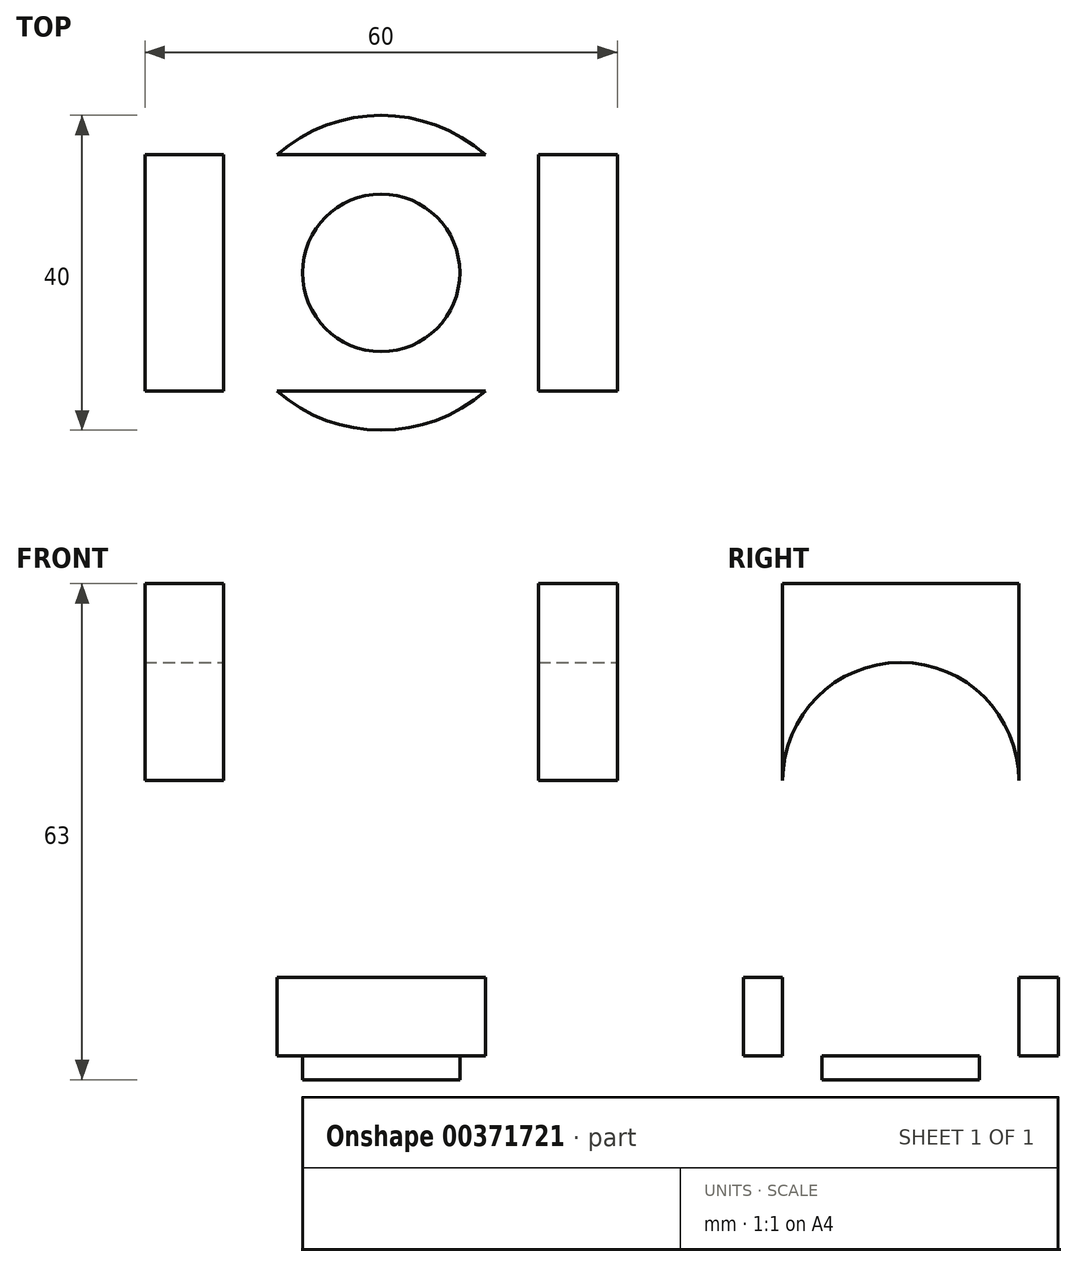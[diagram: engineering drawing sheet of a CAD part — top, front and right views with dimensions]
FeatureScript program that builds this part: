
annotation { "Feature Type Name" : "Feature", "Feature Type Description" : "" }
export const myFeature = defineFeature(function(context is Context, id is Id, definition is map)
    precondition{}
    {
        {
            var Q0;
            Q0=qCreatedBy(makeId("Top.planeOp"),FACE);
            var sketch = newSketch(context, id + "F0", { "sketchPlane" : qUnion([Q0])});
            skCircle(sketch, "E0", {"center": v(0, 0) * mm, "radius": 10 * mm});
            skLineSegment(sketch, "E1", {"start": v(0, 15) * mm, "end": v(-30, 15) * mm});
            skLineSegment(sketch, "E2", {"start": v(-30, 15) * mm, "end": v(-30, -15) * mm});
            skLineSegment(sketch, "E3", {"start": v(30, -15) * mm, "end": v(30, 15) * mm});
            skLineSegment(sketch, "E4", {"start": v(30, 15) * mm, "end": v(0, 15) * mm});
            skLineSegment(sketch, "E5", {"start": v(-30, -15) * mm, "end": v(0, -15) * mm});
            skLineSegment(sketch, "E6", {"start": v(0, -15) * mm, "end": v(30, -15) * mm});
            skCircle(sketch, "E7", {"center": v(0, 0) * mm, "radius": 20 * mm});
            skSolve(sketch);
        }
        {
            var Q0;
            Q0=makeQuery(id+"F0.imprint","IMPRINT",FACE,{"disambiguationData":[TD([[makeQuery(id+"F0.imprint","IMPRINT",EDGE,{"derivedFrom":sQuery(id+"F0.wireOp",EDGE,"E0")}),-1.0]])]});
            var Q1;
            {var subQ0=sQuery(id+"F0.wireOp",EDGE,"E3");Q1=makeQuery(id+"F0.imprint","IMPRINT",FACE,{"disambiguationData":[TD([[makeQuery(id+"F0.imprint","IMPRINT",EDGE,{"derivedFrom":subQ0}),1.0]])]});}
            var Q2;
            {var subQ0=sQuery(id+"F0.wireOp",EDGE,"E2");Q2=makeQuery(id+"F0.imprint","IMPRINT",FACE,{"disambiguationData":[TD([[makeQuery(id+"F0.imprint","IMPRINT",EDGE,{"derivedFrom":subQ0}),1.0]])]});}
            var Q3;
            {var subQ0=sQuery(id+"F0.wireOp",EDGE,"E4");var subQ1=sQuery(id+"F0.wireOp",EDGE,"E1");var subQ2=makeQuery(id+"F0.imprint","INTERSECT",VERTEX,{"derivedFrom":[subQ1,subQ0]});Q3=makeQuery(id+"F0.imprint","IMPRINT",FACE,{"disambiguationData":[TD([[makeQuery(id+"F0.imprint","IMPRINT",EDGE,{"disambiguationData":[TD([[subQ2,-1.0]])],"derivedFrom":subQ1}),-1.0]])]});}
            var Q4;
            {var subQ0=sQuery(id+"F0.wireOp",EDGE,"E6");var subQ1=sQuery(id+"F0.wireOp",EDGE,"E5");var subQ2=makeQuery(id+"F0.imprint","INTERSECT",VERTEX,{"derivedFrom":[subQ1,subQ0]});Q4=makeQuery(id+"F0.imprint","IMPRINT",FACE,{"disambiguationData":[TD([[makeQuery(id+"F0.imprint","IMPRINT",EDGE,{"disambiguationData":[TD([[subQ2,1.0]])],"derivedFrom":subQ1}),-1.0]])]});}
            extrude(context, id + "F1", {"entities" : qUnion([Q0, Q1, Q2, Q3, Q4]), "depth" : 10 * mm});
        }
        {
            var Q0;
            Q0=makeQuery(id+"F1.opExtrude","CAP_FACE",FACE,{"disambiguationData":[OSD([sQuery(id+"F0.wireOp",EDGE,"E0"),sQuery(id+"F0.wireOp",EDGE,"E1"),sQuery(id+"F0.wireOp",EDGE,"E2"),sQuery(id+"F0.wireOp",EDGE,"E3"),sQuery(id+"F0.wireOp",EDGE,"E4"),sQuery(id+"F0.wireOp",EDGE,"E5"),sQuery(id+"F0.wireOp",EDGE,"E6"),sQuery(id+"F0.wireOp",EDGE,"E7")])],"isStart":false});
            var sketch = newSketch(context, id + "F2", { "sketchPlane" : qUnion([Q0])});
            skLineSegment(sketch, "E8", {"start": v(-30, 15) * mm, "end": v(-30, -15) * mm});
            skLineSegment(sketch, "E9", {"start": v(-30, -15) * mm, "end": v(-20, -15) * mm});
            skLineSegment(sketch, "E10", {"start": v(-20, -15) * mm, "end": v(-20, 15) * mm});
            skLineSegment(sketch, "E11", {"start": v(-20, 15) * mm, "end": v(-30, 15) * mm});
            skLineSegment(sketch, "E12", {"start": v(0, 37.06) * mm, "end": v(0, -34.23) * mm, "construction": true});
            skLineSegment(sketch, "E13.MirrorCS", {"start": v(20, 15) * mm, "end": v(30, 15) * mm});
            skLineSegment(sketch, "E14.MirrorCS", {"start": v(20, -15) * mm, "end": v(20, 15) * mm});
            skLineSegment(sketch, "E15.MirrorCS", {"start": v(30, 15) * mm, "end": v(30, -15) * mm});
            skLineSegment(sketch, "E16.MirrorCS", {"start": v(30, -15) * mm, "end": v(20, -15) * mm});
            skSolve(sketch);
        }
        {
            var Q0;
            Q0=makeQuery(id+"F2.imprint","IMPRINT",FACE,{"disambiguationData":[TD([[makeQuery(id+"F2.imprint","IMPRINT",EDGE,{"derivedFrom":sQuery(id+"F2.wireOp",EDGE,"E13.MirrorCS")}),1.0]])]});
            var Q1;
            Q1=makeQuery(id+"F2.imprint","IMPRINT",FACE,{"disambiguationData":[TD([[makeQuery(id+"F2.imprint","IMPRINT",EDGE,{"derivedFrom":sQuery(id+"F2.wireOp",EDGE,"E8")}),1.0]])]});
            extrude(context, id + "F3", {"entities" : qUnion([Q0, Q1]), "operationType" : NewBodyOperationType.ADD, "depth" : 50 * mm});
        }
        {
            var Q0;
            Q0=makeQuery(id+"F3.boolean.opBoolean","MERGE",FACE,{"derivedFrom":[makeQuery(id+"F1.opExtrude","SWEPT_FACE",FACE,{"disambiguationData":[OSD([sQuery(id+"F0.wireOp",EDGE,"E3")])]}),makeQuery(id+"F3.opExtrude","SWEPT_FACE",FACE,{"disambiguationData":[OSD([sQuery(id+"F2.wireOp",EDGE,"E15.MirrorCS")])]})]});
            var sketch = newSketch(context, id + "F4", { "sketchPlane" : qUnion([Q0])});
            skLineSegment(sketch, "E17", {"start": v(0, 65.59) * mm, "end": v(0, -13.6) * mm, "construction": true});
            skPoint(sketch, "E17.endSnap0", {"position": v(0, 60) * mm});
            skArc(sketch, "E18", {"start": v(-15, 35) * mm, "mid": v(0, 50) * mm, "end": v(15, 35) * mm});
            skPoint(sketch, "E19", {"position": v(-15, 30) * mm});
            skCircle(sketch, "E20", {"center": v(0, 35) * mm, "radius": 7.5 * mm});
            skSolve(sketch);
        }
        {
            var Q0;
            {var subQ0=sQuery(id+"F4.wireOp",EDGE,"E18");Q0=makeQuery(id+"F4.imprint","IMPRINT",FACE,{"disambiguationData":[TD([[makeQuery(id+"F4.imprint","IMPRINT",EDGE,{"derivedFrom":subQ0}),1.0]])]});}
            var Q1;
            Q1=makeQuery(id+"F4.imprint","IMPRINT",FACE,{"disambiguationData":[TD([[makeQuery(id+"F4.imprint","IMPRINT",EDGE,{"derivedFrom":sQuery(id+"F4.wireOp",EDGE,"E20")}),1.0]])]});
            extrude(context, id + "F5", {"entities" : qUnion([Q0, Q1]), "operationType" : NewBodyOperationType.REMOVE, "endBound" : BoundingType.THROUGH_ALL, "oppositeDirection" : true, "depth" : 25 * mm});
        }
        {
            var Q0;
            Q0=makeQuery(id+"F1.opExtrude","CAP_FACE",FACE,{"disambiguationData":[OSD([sQuery(id+"F0.wireOp",EDGE,"E0"),sQuery(id+"F0.wireOp",EDGE,"E1"),sQuery(id+"F0.wireOp",EDGE,"E2"),sQuery(id+"F0.wireOp",EDGE,"E3"),sQuery(id+"F0.wireOp",EDGE,"E4"),sQuery(id+"F0.wireOp",EDGE,"E5"),sQuery(id+"F0.wireOp",EDGE,"E6"),sQuery(id+"F0.wireOp",EDGE,"E7")])],"isStart":true});
            var sketch = newSketch(context, id + "F6", { "sketchPlane" : qUnion([Q0])});
            skCircle(sketch, "E21", {"center": v(0, 0) * mm, "radius": 10 * mm});
            skCircle(sketch, "E22", {"center": v(0, 0) * mm, "radius": 17 * mm});
            skSolve(sketch);
        }
        {
            var Q0;
            Q0=makeQuery(id+"F6.imprint","IMPRINT",FACE,{"disambiguationData":[TD([[makeQuery(id+"F6.imprint","IMPRINT",EDGE,{"derivedFrom":sQuery(id+"F6.wireOp",EDGE,"E21")}),1.0]])]});
            extrude(context, id + "F7", {"entities" : qUnion([Q0]), "operationType" : NewBodyOperationType.ADD, "depth" : 3 * mm});
        }
    });
